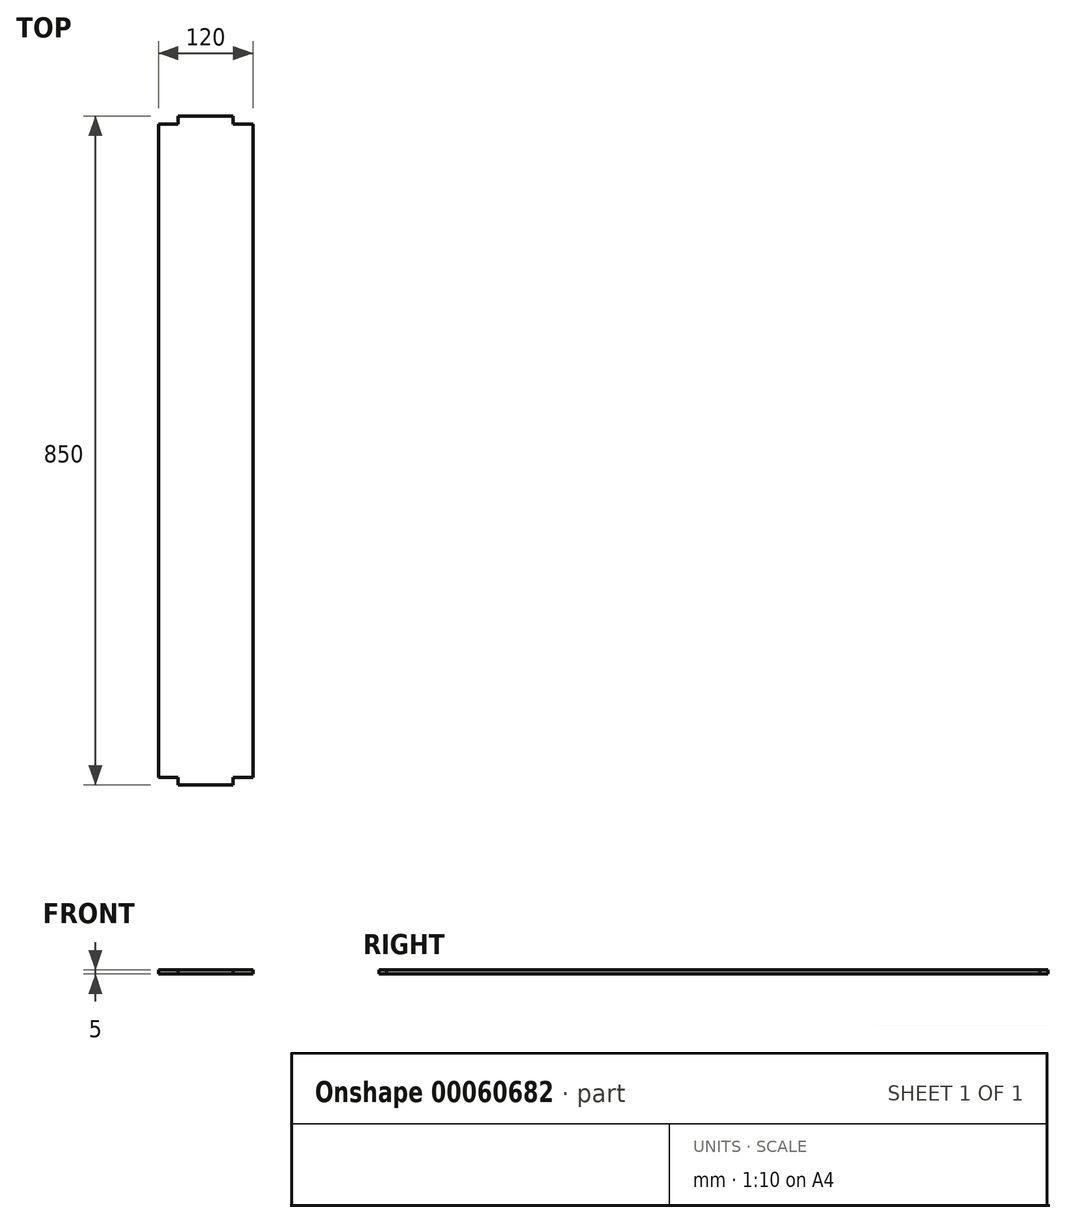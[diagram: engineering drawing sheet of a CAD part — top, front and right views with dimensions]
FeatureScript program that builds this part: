
annotation { "Feature Type Name" : "Feature", "Feature Type Description" : "" }
export const myFeature = defineFeature(function(context is Context, id is Id, definition is map)
    precondition{}
    {
        {
            var Q0;
            Q0=qCreatedBy(makeId("Front.planeOp"),FACE);
            var sketch = newSketch(context, id + "F0", { "sketchPlane" : qUnion([Q0])});
            skLineSegment(sketch, "E0.bottom", {"start": v(-60, 0) * mm, "end": v(0, 0) * mm});
            skLineSegment(sketch, "E0.top", {"start": v(-60, 5) * mm, "end": v(0, 5) * mm});
            skLineSegment(sketch, "E0.left", {"start": v(-60, 0) * mm, "end": v(-60, 5) * mm});
            skLineSegment(sketch, "E0.right", {"start": v(0, 0) * mm, "end": v(0, 5) * mm, "construction": true});
            skLineSegment(sketch, "E1.MirrorCS", {"start": v(60, 5) * mm, "end": v(0, 5) * mm});
            skLineSegment(sketch, "E2.MirrorCS", {"start": v(60, 0) * mm, "end": v(60, 5) * mm});
            skLineSegment(sketch, "E3.MirrorCS", {"start": v(60, 0) * mm, "end": v(0, 0) * mm});
            skSolve(sketch);
        }
        {
            var Q0;
            Q0=makeQuery(id+"F0.imprint","IMPRINT",FACE,{"disambiguationData":[TD([[makeQuery(id+"F0.imprint","IMPRINT",EDGE,{"derivedFrom":sQuery(id+"F0.wireOp",EDGE,"E0.bottom")}),1.0]])]});
            extrude(context, id + "F1", {"entities" : qUnion([Q0]), "endBound" : BoundingType.SYMMETRIC, "depth" : 850 * mm});
        }
        {
            var Q0;
            Q0=makeQuery(id+"F1.opExtrude","SWEPT_FACE",FACE,{"disambiguationData":[OSD([sQuery(id+"F0.wireOp",EDGE,"E0.top"),sQuery(id+"F0.wireOp",EDGE,"E1.MirrorCS")])]});
            var sketch = newSketch(context, id + "F2", { "sketchPlane" : qUnion([Q0])});
            skLineSegment(sketch, "E4.bottom", {"start": v(60, -425) * mm, "end": v(35, -425) * mm});
            skLineSegment(sketch, "E4.top", {"start": v(60, -415) * mm, "end": v(35, -415) * mm});
            skLineSegment(sketch, "E4.left", {"start": v(60, -425) * mm, "end": v(60, -415) * mm});
            skLineSegment(sketch, "E4.right", {"start": v(35, -425) * mm, "end": v(35, -415) * mm});
            skLineSegment(sketch, "E5.bottom", {"start": v(-60, -425) * mm, "end": v(-35, -425) * mm});
            skLineSegment(sketch, "E5.top", {"start": v(-60, -415) * mm, "end": v(-35, -415) * mm});
            skLineSegment(sketch, "E5.left", {"start": v(-60, -425) * mm, "end": v(-60, -415) * mm});
            skLineSegment(sketch, "E5.right", {"start": v(-35, -425) * mm, "end": v(-35, -415) * mm});
            skLineSegment(sketch, "E6", {"start": v(60, 0) * mm, "end": v(-60, 0) * mm, "construction": true});
            skLineSegment(sketch, "E7.MirrorCS", {"start": v(-35, 425) * mm, "end": v(-35, 415) * mm});
            skLineSegment(sketch, "E8.MirrorCS", {"start": v(-60, 425) * mm, "end": v(-60, 415) * mm});
            skLineSegment(sketch, "E9.MirrorCS", {"start": v(35, 425) * mm, "end": v(35, 415) * mm});
            skLineSegment(sketch, "E10.MirrorCS", {"start": v(60, 425) * mm, "end": v(60, 415) * mm});
            skLineSegment(sketch, "E11.MirrorCS", {"start": v(-60, 415) * mm, "end": v(-35, 415) * mm});
            skLineSegment(sketch, "E12.MirrorCS", {"start": v(-60, 425) * mm, "end": v(-35, 425) * mm});
            skLineSegment(sketch, "E13.MirrorCS", {"start": v(60, 415) * mm, "end": v(35, 415) * mm});
            skLineSegment(sketch, "E14.MirrorCS", {"start": v(60, 425) * mm, "end": v(35, 425) * mm});
            skSolve(sketch);
        }
        {
            var Q0;
            Q0 = qSketchRegion(id + "F2", true);
            extrude(context, id + "F3", {"entities" : qUnion([Q0]), "operationType" : NewBodyOperationType.REMOVE, "endBound" : BoundingType.THROUGH_ALL, "oppositeDirection" : true, "depth" : 25 * mm});
        }
    });
